# Revit family: Enave P 180_240_Eng
name_source: partatom
category: Оборудование
units: mm (PartAtom-declared; Revit-internal decimal feet)

## family parameters
Всегда вертикально = Да
Классификация = Нет
На основе рабочей плоскости = Нет
Общий = Нет
При загрузке вырезать с полостями = Нет
Размер круглого соединителя = Использовать диаметр
Тип детали = Нормальный
Точка принадлежности помещению = Нет

## types (4) — shared parameters
00_20_Manufacturer = Vents
00_20_Name = Air handling unit
Casing Material = Polypropylene (black)
D = 160 мм
Diameter = 160 мм
Filter = Coarse > 60%
H = 290 мм
Height = 290 мм
L = 1060 мм
Length = 1060 мм
Lk = 930 мм
Load Classification = HVAC
Maintenance zone material = <По категории>
Number of Fase = 1
Pressure_Static_Air = 0.0 Па
Temperature of moving air = +45°С
Voltage = 230 В
W = 677 мм
Width = 677 мм
Wk = 640 мм
d = 150 мм
wd1 = 134 мм
wd2 = 300 мм
Изготовитель = Vents
zero-valued in all types: Отметка по умолчанию

## per-type parameters (varying)
| type | Amperage | Maximum Air Flow | Power | Sound pressure level at 3 m distance | Weight |
| Enave 180 P | 0.490 А | 181.0 м³/ч | 53 Вт | 29 dBA | 12.00 кг |
| Enave-T 180 P | 0.490 А | 181.0 м³/ч | 53 Вт | 29 dBA | 15.00 кг |
| Enave 240 P | 1.340 А | 310.0 м³/ч | 171 Вт | 33 dBA | 12.00 кг |
| Enave-T 240 P | 1.340 А | 310.0 м³/ч | 171 Вт | 33 dBA | 15.00 кг |

note: column(s) folded — value = type name in every type: 00_20_Type
